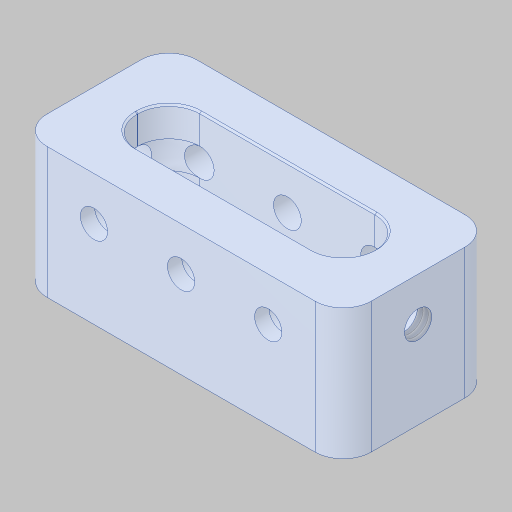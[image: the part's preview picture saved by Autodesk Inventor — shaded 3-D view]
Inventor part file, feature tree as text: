
AUTODESK INVENTOR PART (.ipt)
format: ipt  version: 2023.5 (Build 275446000, 446)  size: 358,400 bytes
history: native  units: in
note: dims shown in document units (in); Inventor stores cm internally (conversion verified against a paired STEP export)
features: sketch x4, hole x3, projected_geometry x2, extrude x1, chamfer x1
ambient origin geometry x8: Origin, YZ Plane, XZ Plane, XY Plane, X Axis, Y Axis, Z Axis, Center Point
bodies: Solid1 (feature_tree)
feature tree (11):
  extrude  "Extrusion1"  Depth=1.0in TaperAngle=0.0deg
  hole  "Hole1"  [1 undecoded]
  hole  "Hole2"  [1 undecoded]
  hole  "Hole3"  [1 undecoded]
  sketch  "Sketch1"  dims[d0=0.0625in d1=1.0in d2=0.0in]
  projected_geometry  "Projected Loop1"
  sketch  "Sketch2"  dims[d3=0.156in d4=0.38in d5=0.385in d6=0.25in d7=0.563in d8=1.0in d9=0.8108in]
  projected_geometry  "Projected Loop2"
  sketch  "Sketch3"  dims[d10=0.196in d11=0.5in d12=0.375in d13=0.25in d14=0.5635in d15=1.0in d16=0.8108in]
  sketch  "Sketch4"  dims[d17=0.156in d18=0.38in d19=0.385in d20=0.25in d21=0.563in d22=1.0in d23=0.8108in]
  chamfer  "Chamfer2"  [1 undecoded]
note: 4 required parameter values undecoded (feature->parameter linkage not recoverable at this tier; creation-order binding heuristic only, values carry confidence <= 0.55)
